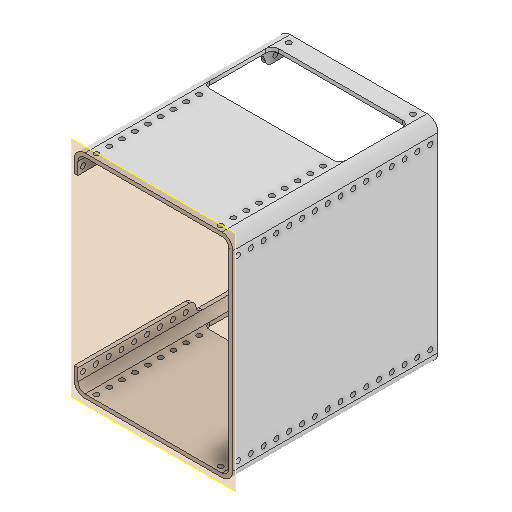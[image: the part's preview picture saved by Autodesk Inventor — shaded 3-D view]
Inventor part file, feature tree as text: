
AUTODESK INVENTOR PART (.ipt)
format: ipt  version: 2022 (Build 260153000, 153)  size: 369,152 bytes
history: native  units: mm
features: projected_geometry x6, sketch x5, reference x5, extrude x3, hole x2, fillet x2, other x2, plane x1, pattern_linear x1
ambient origin geometry x8: Origin, YZ Plane, XZ Plane, XY Plane, X Axis, Y Axis, Z Axis, Center Point
bodies: Volumenkörper1 (feature_tree)
feature tree (27):
  plane  "Arbeitsebene1"
  extrude  "Extrusion1"  Depth=3.0mm
  hole  "Bohrung1"  [1 undecoded]
  hole  "Bohrung2"  [1 undecoded]
  pattern_linear  "Rechteckige Anordnung1"  Spacing1=15.0mm  [1 undecoded]
  extrude  "Extrusion2"  Depth=5.0mm
  fillet  "Rundung1"  [1 undecoded]
  extrude  "Extrusion3"  Depth=5.0mm
  fillet  "Rundung2"  [1 undecoded]
  sketch  "Skizze1"  dims[d0=0.5mm d1=3.0mm]
  reference  "Referenz1"
  sketch  "Skizze2"  dims[d2=160.0mm d3=0.0mm]
  reference  "Referenz2"
  reference  "Referenz3"
  sketch  "Skizze3"  dims[d4=4.0mm d5=6.0mm d6=4.0mm d7=2.0mm d8=90.0deg d9=8.0mm d10=20.594885mm]
  reference  "Referenz4"
  reference  "Referenz5"
  sketch  "Skizze4"  dims[d11=4.0mm d12=6.0mm d13=4.0mm d14=2.0mm d15=90.0deg d16=8.0mm d17=20.594885mm d18=160.0mm d20=10.0mm]
  projected_geometry  "Projizierte Kontur1"
  projected_geometry  "Projizierte Kontur2"
  sketch  "Skizze5"  dims[d21=18.0mm d22=18.0mm d23=15.0mm d24=0.0mm d25=5.0mm d26=0.0mm d27=0.0mm d28=5.0mm]
  projected_geometry  "Projizierte Kontur3"
  projected_geometry  "Projizierte Kontur4"
  projected_geometry  "Projizierte Kontur5"
  projected_geometry  "Projizierte Kontur6"
  other  "Omnicscope_Xiao.iam"
  other  "Omniscope_USBC_Base:1"
note: 5 required parameter values undecoded (feature->parameter linkage not recoverable at this tier; creation-order binding heuristic only, values carry confidence <= 0.55)
